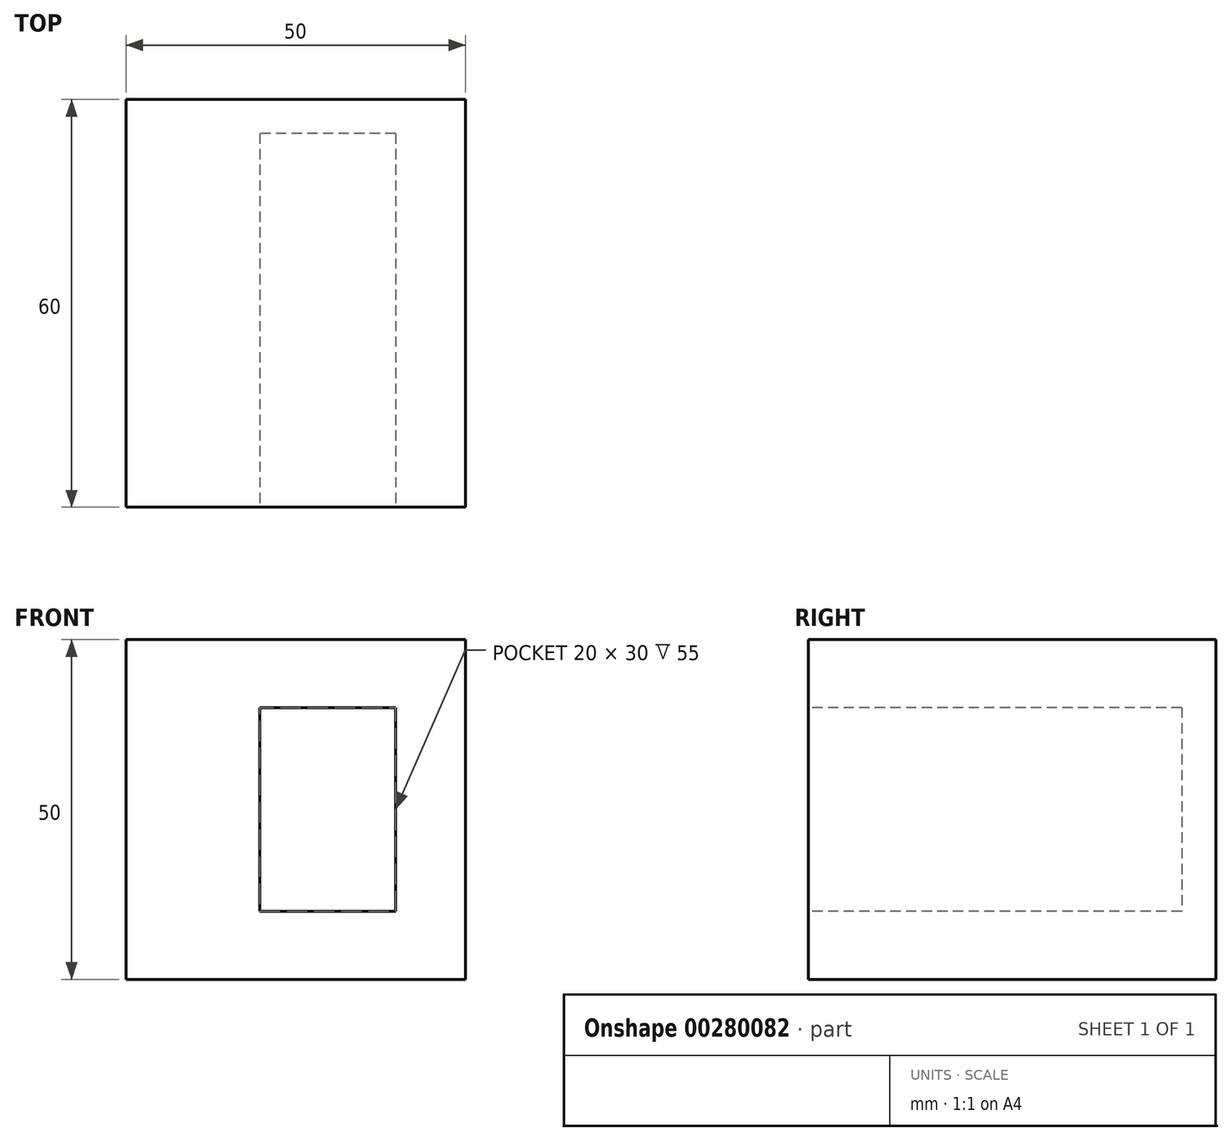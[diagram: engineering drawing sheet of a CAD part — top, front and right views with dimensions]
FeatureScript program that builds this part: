
annotation { "Feature Type Name" : "Feature", "Feature Type Description" : "" }
export const myFeature = defineFeature(function(context is Context, id is Id, definition is map)
    precondition{}
    {
        {
            var Q0;
            Q0=qCreatedBy(makeId("Front.planeOp"),FACE);
            var sketch = newSketch(context, id + "F0", { "sketchPlane" : qUnion([Q0])});
            skLineSegment(sketch, "E0.bottom", {"start": v(0, 0) * mm, "end": v(50, 0) * mm});
            skLineSegment(sketch, "E0.top", {"start": v(0, 50) * mm, "end": v(50, 50) * mm});
            skLineSegment(sketch, "E0.left", {"start": v(0, 0) * mm, "end": v(0, 50) * mm});
            skLineSegment(sketch, "E0.right", {"start": v(50, 0) * mm, "end": v(50, 50) * mm});
            skSolve(sketch);
        }
        {
            var Q0;
            Q0 = qSketchRegion(id + "F0", true);
            extrude(context, id + "F1", {"entities" : qUnion([Q0]), "depth" : 60 * mm});
        }
        {
            var Q0;
            Q0=makeQuery(id+"F1.opExtrude","CAP_FACE",FACE,{"disambiguationData":[OSD([sQuery(id+"F0.wireOp",EDGE,"E0.bottom"),sQuery(id+"F0.wireOp",EDGE,"E0.top"),sQuery(id+"F0.wireOp",EDGE,"E0.left"),sQuery(id+"F0.wireOp",EDGE,"E0.right")])],"isStart":false});
            var sketch = newSketch(context, id + "F2", { "sketchPlane" : qUnion([Q0])});
            skLineSegment(sketch, "E1.bottom", {"start": v(39.72, 40) * mm, "end": v(19.72, 40) * mm});
            skLineSegment(sketch, "E1.top", {"start": v(39.72, 10) * mm, "end": v(19.72, 10) * mm});
            skLineSegment(sketch, "E1.left", {"start": v(39.72, 40) * mm, "end": v(39.72, 10) * mm});
            skLineSegment(sketch, "E1.right", {"start": v(19.72, 40) * mm, "end": v(19.72, 10) * mm});
            skPoint(sketch, "E1.middle", {"position": v(29.72, 25) * mm});
            skSolve(sketch);
        }
        {
            var Q0;
            Q0 = qSketchRegion(id + "F2", true);
            extrude(context, id + "F3", {"entities" : qUnion([Q0]), "operationType" : NewBodyOperationType.REMOVE, "oppositeDirection" : true, "depth" : 55 * mm});
        }
    });
